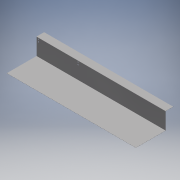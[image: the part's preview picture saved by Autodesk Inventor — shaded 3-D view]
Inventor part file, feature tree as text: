
AUTODESK INVENTOR PART (.ipt)
format: ipt  version: 2016 (Build 200138000, 138)  size: 187,392 bytes
history: native  units: mm
features: sheet_metal_op x7, sketch x4, other x4, hole x1
ambient origin geometry x8: Origin, YZ Plane, XZ Plane, XY Plane, X Axis, Y Axis, Z Axis, Center Point
bodies: Solid1 (feature_tree)
feature tree (16):
  sheet_metal_op  "Face1"
  sheet_metal_op  "Flange1"
  sheet_metal_op  "Flange2"
  hole  "Hole1"  [1 undecoded]
  sketch  "Sketch1"  dims[d0=392.0mm d1=1695.0mm]
  other  "Plate1"
  sketch  "Sketch2"  dims[d2=1.6mm]
  other  "Plate2"
  sheet_metal_op  "Bend1"
  sheet_metal_op  "Corner1"
  sketch  "Sketch3"  dims[d3=1.6mm]
  other  "Plate3"
  sheet_metal_op  "Bend2"
  sheet_metal_op  "Corner2"
  sketch  "Sketch4"  dims[d4=0.8mm d5=3.2mm d6=1.6mm d7=223.0mm d8=90.0deg d9=1.6mm d10=6.4mm d11=1.6mm d12=1.6mm d13=1.6mm d14=0.8mm d15=3.2mm d16=1.6mm d17=70.0mm d18=-15.707963mm d19=1.6mm d20=6.4mm d21=1.6mm d22=1.6mm d23=60.0mm d24=12.0mm d25=12.0mm d26=25.0mm d27=25.0mm d28=15.0mm d29=15.0mm d30=12.0mm d31=12.0mm d34=12.0mm d35=6.0mm d36=4.0mm d37=2.0mm d38=90.0deg d39=1.6mm d40=20.594885mm d41=570.0mm d42=15.0mm d43=15.0mm d44=25.0mm d45=25.0mm]
  other  "Definition1"
note: 1 required parameter value undecoded (feature->parameter linkage not recoverable at this tier; creation-order binding heuristic only, values carry confidence <= 0.55)
